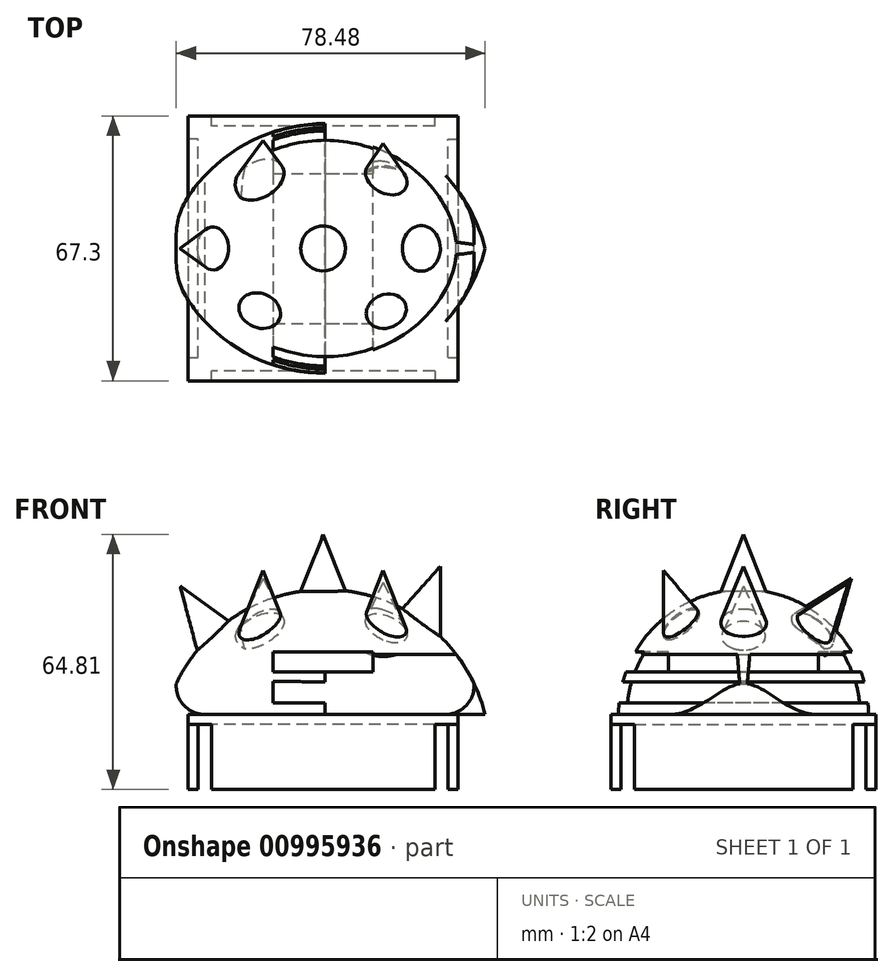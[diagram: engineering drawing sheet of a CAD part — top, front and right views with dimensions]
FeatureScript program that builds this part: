
annotation { "Feature Type Name" : "Feature", "Feature Type Description" : "" }
export const myFeature = defineFeature(function(context is Context, id is Id, definition is map)
    precondition{}
    {
        {
            var Q0;
            Q0=qCreatedBy(makeId("Front.planeOp"),FACE);
            var sketch = newSketch(context, id + "F0", { "sketchPlane" : qUnion([Q0])});
            skLineSegment(sketch, "E0", {"start": v(-40.15, 0) * mm, "end": v(41.13, 0) * mm});
            skLineSegment(sketch, "E1", {"start": v(0, 0) * mm, "end": v(0, 31.75) * mm});
            skArc(sketch, "E2", {"start": v(41.13, 0) * mm, "mid": v(0.5, 31.75) * mm, "end": v(-40.15, 0) * mm});
            skSolve(sketch);
        }
        {
            var Q0;
            {var subQ3=sQuery(id+"F0.wireOp",EDGE,"E1");Q0=makeQuery(id+"F0.imprint","IMPRINT",FACE,{"disambiguationData":[TD([[makeQuery(id+"F0.imprint","IMPRINT",EDGE,{"derivedFrom":subQ3}),-1.0]])]});}
            var Q1;
            {var subQ3=sQuery(id+"F0.wireOp",EDGE,"E1");Q1=makeQuery(id+"F0.imprint","IMPRINT",FACE,{"disambiguationData":[TD([[makeQuery(id+"F0.imprint","IMPRINT",EDGE,{"derivedFrom":subQ3}),1.0]])]});}
            var Q2;
            Q2=sQuery(id+"F0.wireOp",EDGE,"E0");
            revolve(context, id + "F1", {"surfaceOperationType" : NewSurfaceOperationType.NEW, "entities" : qUnion([Q0, Q1]), "axis" : qUnion([Q2]), "revolveType" : RevolveType.TWO_DIRECTIONS, "angle" : 90 * degree, "angleBack" : 270 * degree});
        }
        {
            var Q0;
            Q0=qCreatedBy(makeId("Front.planeOp"),FACE);
            var sketch = newSketch(context, id + "F2", { "sketchPlane" : qUnion([Q0])});
            skLineSegment(sketch, "E3.0.0", {"start": v(41.13, 0) * mm, "end": v(-40.15, 0) * mm});
            skLineSegment(sketch, "E3.0.1", {"start": v(-40.15, 0) * mm, "end": v(41.13, 0) * mm});
            skArc(sketch, "E4", {"start": v(41.13, 0) * mm, "mid": v(0.5, 31.65) * mm, "end": v(-40.15, 0) * mm});
            skArc(sketch, "E5", {"start": v(-37.33, 7.8) * mm, "mid": v(-35.4, 2.32) * mm, "end": v(-30.07, 0) * mm});
            skLineSegment(sketch, "E6", {"start": v(0.5, -10.26) * mm, "end": v(0.5, 25.68) * mm});
            skArc(sketch, "E7.MirrorCS", {"start": v(38.32, 7.8) * mm, "mid": v(36.38, 2.32) * mm, "end": v(31.06, 0) * mm});
            skLineSegment(sketch, "E8", {"start": v(-32.75, 15.27) * mm, "end": v(33.73, 15.27) * mm});
            skSolve(sketch);
        }
        {
            var Q0;
            {var subQ3=sQuery(id+"F2.wireOp",EDGE,"E7.MirrorCS");Q0=makeQuery(id+"F2.imprint","IMPRINT",FACE,{"disambiguationData":[TD([[makeQuery(id+"F2.imprint","IMPRINT",EDGE,{"derivedFrom":subQ3}),1.0]])]});}
            var Q1;
            {var subQ3=sQuery(id+"F2.wireOp",EDGE,"E5");Q1=makeQuery(id+"F2.imprint","IMPRINT",FACE,{"disambiguationData":[TD([[makeQuery(id+"F2.imprint","IMPRINT",EDGE,{"derivedFrom":subQ3}),-1.0]])]});}
            extrude(context, id + "F3", {"entities" : qUnion([Q0, Q1]), "operationType" : NewBodyOperationType.REMOVE, "endBound" : BoundingType.SYMMETRIC, "depth" : 127 * mm, "offsetDistance" : 25.4 * mm});
        }
        {
            var Q0;
            Q0=qCreatedBy(makeId("Top.planeOp"),FACE);
            var sketch = newSketch(context, id + "F4", { "sketchPlane" : qUnion([Q0])});
            skLineSegment(sketch, "E9.bottom", {"start": v(34.3, 33.66) * mm, "end": v(-34.3, 33.66) * mm});
            skLineSegment(sketch, "E9.top", {"start": v(34.3, -33.66) * mm, "end": v(-34.3, -33.66) * mm});
            skLineSegment(sketch, "E9.left", {"start": v(34.3, 33.66) * mm, "end": v(34.3, -33.66) * mm});
            skLineSegment(sketch, "E9.right", {"start": v(-34.3, 33.66) * mm, "end": v(-34.3, -33.66) * mm});
            skPoint(sketch, "E9.middle", {"position": v(0, 0) * mm});
            skSolve(sketch);
        }
        {
            var Q0;
            Q0=makeQuery(id+"F4.imprint","IMPRINT",FACE,{"disambiguationData":[TD([[makeQuery(id+"F4.imprint","IMPRINT",EDGE,{"derivedFrom":sQuery(id+"F4.wireOp",EDGE,"E9.bottom")}),1.0]])]});
            extrude(context, id + "F5", {"entities" : qUnion([Q0]), "operationType" : NewBodyOperationType.ADD, "oppositeDirection" : true, "depth" : 2.54 * mm, "offsetDistance" : 25.4 * mm});
        }
        {
            var Q0;
            Q0=makeQuery(id+"F5.opExtrude","CAP_FACE",FACE,{"disambiguationData":[OSD([sQuery(id+"F4.wireOp",EDGE,"E9.bottom"),sQuery(id+"F4.wireOp",EDGE,"E9.top"),sQuery(id+"F4.wireOp",EDGE,"E9.left"),sQuery(id+"F4.wireOp",EDGE,"E9.right")])],"isStart":false});
            var sketch = newSketch(context, id + "F6", { "sketchPlane" : qUnion([Q0])});
            skLineSegment(sketch, "E10.bottom", {"start": v(31.75, 31.12) * mm, "end": v(-31.75, 31.12) * mm});
            skLineSegment(sketch, "E10.top", {"start": v(31.75, -31.12) * mm, "end": v(-31.75, -31.12) * mm});
            skLineSegment(sketch, "E10.left", {"start": v(31.75, 31.12) * mm, "end": v(31.75, -31.12) * mm});
            skLineSegment(sketch, "E10.right", {"start": v(-31.75, 31.12) * mm, "end": v(-31.75, -31.12) * mm});
            skPoint(sketch, "E10.middle", {"position": v(0, 0) * mm});
            skLineSegment(sketch, "E11.0.0", {"start": v(34.3, 33.66) * mm, "end": v(-34.3, 33.66) * mm});
            skLineSegment(sketch, "E11.0.1", {"start": v(-34.3, 33.66) * mm, "end": v(-34.3, -33.66) * mm});
            skLineSegment(sketch, "E11.0.2", {"start": v(-34.3, -33.66) * mm, "end": v(34.3, -33.66) * mm});
            skLineSegment(sketch, "E11.0.3", {"start": v(34.3, -33.66) * mm, "end": v(34.3, 33.66) * mm});
            skSolve(sketch);
        }
        {
            var Q0;
            Q0=makeQuery(id+"F6.imprint","IMPRINT",FACE,{"disambiguationData":[TD([[makeQuery(id+"F6.imprint","IMPRINT",EDGE,{"derivedFrom":sQuery(id+"F6.wireOp",EDGE,"E10.bottom")}),-1.0]])]});
            extrude(context, id + "F7", {"entities" : qUnion([Q0]), "operationType" : NewBodyOperationType.ADD, "depth" : 16.5 * mm, "offsetDistance" : 25.4 * mm});
        }
        {
            var Q0;
            Q0=makeQuery(id+"F7.opExtrude","CAP_FACE",FACE,{"disambiguationData":[OSD([sQuery(id+"F6.wireOp",EDGE,"E10.bottom"),sQuery(id+"F6.wireOp",EDGE,"E10.top"),sQuery(id+"F6.wireOp",EDGE,"E10.left"),sQuery(id+"F6.wireOp",EDGE,"E10.right"),sQuery(id+"F6.wireOp",EDGE,"E11.0.0"),sQuery(id+"F6.wireOp",EDGE,"E11.0.1"),sQuery(id+"F6.wireOp",EDGE,"E11.0.2"),sQuery(id+"F6.wireOp",EDGE,"E11.0.3")])],"isStart":false});
            var sketch = newSketch(context, id + "F8", { "sketchPlane" : qUnion([Q0])});
            skLineSegment(sketch, "E12.0.0", {"start": v(34.3, -33.66) * mm, "end": v(34.3, 33.66) * mm});
            skLineSegment(sketch, "E12.0.1", {"start": v(34.3, 33.66) * mm, "end": v(-34.3, 33.66) * mm});
            skLineSegment(sketch, "E12.0.2", {"start": v(-34.3, 33.66) * mm, "end": v(-34.3, -33.66) * mm});
            skLineSegment(sketch, "E12.0.3", {"start": v(-34.3, -33.66) * mm, "end": v(34.3, -33.66) * mm});
            skLineSegment(sketch, "E13.0", {"start": v(31.75, 31.12) * mm, "end": v(-31.75, 31.12) * mm});
            skLineSegment(sketch, "E14.0", {"start": v(31.75, 31.12) * mm, "end": v(31.75, -31.12) * mm});
            skLineSegment(sketch, "E15.0.0", {"start": v(31.75, -31.12) * mm, "end": v(31.75, 31.12) * mm});
            skLineSegment(sketch, "E15.0.2", {"start": v(-31.75, 31.12) * mm, "end": v(-31.75, -31.12) * mm});
            skLineSegment(sketch, "E15.0.3", {"start": v(-31.75, -31.12) * mm, "end": v(31.75, -31.12) * mm});
            skLineSegment(sketch, "E16", {"start": v(31.75, 27.74) * mm, "end": v(34.3, 27.74) * mm});
            skLineSegment(sketch, "E17", {"start": v(28.37, 31.12) * mm, "end": v(28.37, 33.66) * mm});
            skLineSegment(sketch, "E18", {"start": v(-34.3, 27.74) * mm, "end": v(-31.75, 27.74) * mm});
            skLineSegment(sketch, "E19", {"start": v(-28.37, 33.66) * mm, "end": v(-28.37, 31.12) * mm});
            skLineSegment(sketch, "E20", {"start": v(-31.75, -27.74) * mm, "end": v(-34.3, -27.74) * mm});
            skLineSegment(sketch, "E21", {"start": v(-28.37, -31.12) * mm, "end": v(-28.37, -33.66) * mm});
            skLineSegment(sketch, "E22", {"start": v(31.75, -27.74) * mm, "end": v(34.3, -27.74) * mm});
            skLineSegment(sketch, "E23", {"start": v(28.37, -31.12) * mm, "end": v(28.37, -33.66) * mm});
            skSolve(sketch);
        }
        {
            var Q0;
            {var subQ4=sQuery(id+"F8.wireOp",EDGE,"E22");Q0=makeQuery(id+"F8.imprint","IMPRINT",FACE,{"disambiguationData":[TD([[makeQuery(id+"F8.imprint","IMPRINT",EDGE,{"derivedFrom":subQ4}),-1.0]])]});}
            var Q1;
            {var subQ7=sQuery(id+"F8.wireOp",EDGE,"E16");Q1=makeQuery(id+"F8.imprint","IMPRINT",FACE,{"disambiguationData":[TD([[makeQuery(id+"F8.imprint","IMPRINT",EDGE,{"derivedFrom":subQ7}),1.0]])]});}
            var Q2;
            {var subQ4=sQuery(id+"F8.wireOp",EDGE,"E18");Q2=makeQuery(id+"F8.imprint","IMPRINT",FACE,{"disambiguationData":[TD([[makeQuery(id+"F8.imprint","IMPRINT",EDGE,{"derivedFrom":subQ4}),1.0]])]});}
            var Q3;
            {var subQ4=sQuery(id+"F8.wireOp",EDGE,"E20");Q3=makeQuery(id+"F8.imprint","IMPRINT",FACE,{"disambiguationData":[TD([[makeQuery(id+"F8.imprint","IMPRINT",EDGE,{"derivedFrom":subQ4}),1.0]])]});}
            extrude(context, id + "F9", {"entities" : qUnion([Q0, Q1, Q2, Q3]), "operationType" : NewBodyOperationType.REMOVE, "oppositeDirection" : true, "depth" : 16.5 * mm, "offsetDistance" : 25.4 * mm});
        }
        {
            var Q0;
            Q0=qCreatedBy(makeId("Front.planeOp"),FACE);
            var sketch = newSketch(context, id + "F10", { "sketchPlane" : qUnion([Q0])});
            skPoint(sketch, "E24.middle", {"position": v(0, 12.77) * mm});
            skLineSegment(sketch, "E25", {"start": v(12.7, 10.84) * mm, "end": v(12.7, 15.92) * mm});
            skLineSegment(sketch, "E26.MirrorCS", {"start": v(-12.7, 10.84) * mm, "end": v(-12.7, 15.92) * mm});
            skLineSegment(sketch, "E27", {"start": v(-12.7, 10.84) * mm, "end": v(12.7, 10.84) * mm});
            skLineSegment(sketch, "E28", {"start": v(-12.7, 15.92) * mm, "end": v(12.7, 15.92) * mm});
            skPoint(sketch, "E29", {"position": v(0, 10.84) * mm});
            skSolve(sketch);
        }
        {
            var Q0;
            Q0=makeQuery(id+"F10.imprint","IMPRINT",FACE,{"disambiguationData":[TD([[makeQuery(id+"F10.imprint","IMPRINT",EDGE,{"derivedFrom":sQuery(id+"F10.wireOp",EDGE,"E25")}),1.0]])]});
            extrude(context, id + "F11", {"entities" : qUnion([Q0]), "operationType" : NewBodyOperationType.REMOVE, "endBound" : BoundingType.SYMMETRIC, "oppositeDirection" : true, "depth" : 76.2 * mm, "offsetDistance" : 25.4 * mm});
        }
        {
            var Q0;
            Q0=makeQuery(id+"F10.imprint","IMPRINT",FACE,{"disambiguationData":[TD([[makeQuery(id+"F10.imprint","IMPRINT",EDGE,{"derivedFrom":sQuery(id+"F10.wireOp",EDGE,"E25")}),1.0]])]});
            extrude(context, id + "F12", {"entities" : qUnion([Q0]), "operationType" : NewBodyOperationType.ADD, "endBound" : BoundingType.SYMMETRIC, "depth" : 38.1 * mm, "offsetDistance" : 25.4 * mm});
        }
        {
            var Q0;
            Q0=qCreatedBy(makeId("Front.planeOp"),FACE);
            var sketch = newSketch(context, id + "F13", { "sketchPlane" : qUnion([Q0])});
            skLineSegment(sketch, "E30", {"start": v(-12.7, 8.43) * mm, "end": v(-12.7, 2.93) * mm});
            skLineSegment(sketch, "E31", {"start": v(-12.7, 2.93) * mm, "end": v(12.74, 2.93) * mm});
            skLineSegment(sketch, "E32", {"start": v(12.74, 2.93) * mm, "end": v(12.74, 8.12) * mm});
            skLineSegment(sketch, "E33", {"start": v(12.74, 8.12) * mm, "end": v(-12.7, 8.43) * mm});
            skSolve(sketch);
        }
        {
            var Q0;
            Q0 = qSketchRegion(id + "F13", true);
            extrude(context, id + "F14", {"entities" : qUnion([Q0]), "operationType" : NewBodyOperationType.REMOVE, "oppositeDirection" : true, "depth" : 76.2 * mm, "offsetDistance" : 25.4 * mm});
        }
        {
            var Q0;
            Q0=makeQuery(id+"F14.boolean.opBoolean","COPY",FACE,{"derivedFrom":makeQuery(id+"F14.opExtrude","CAP_FACE",FACE,{"disambiguationData":[OSD([sQuery(id+"F13.wireOp",EDGE,"E30"),sQuery(id+"F13.wireOp",EDGE,"E31"),sQuery(id+"F13.wireOp",EDGE,"E32"),sQuery(id+"F13.wireOp",EDGE,"E33")])],"isStart":true})});
            extrude(context, id + "F15", {"entities" : qUnion([Q0]), "operationType" : NewBodyOperationType.REMOVE, "oppositeDirection" : true, "depth" : 50.8 * mm, "offsetDistance" : 25.4 * mm});
        }
        {
            var Q0;
            Q0=qCreatedBy(makeId("Front.planeOp"),FACE);
            var sketch = newSketch(context, id + "F16", { "sketchPlane" : qUnion([Q0])});
            skLineSegment(sketch, "E34", {"start": v(0, 27.42) * mm, "end": v(0, 45.76) * mm});
            skLineSegment(sketch, "E35", {"start": v(0, 45.76) * mm, "end": v(-7.24, 27.42) * mm});
            skLineSegment(sketch, "E36", {"start": v(-7.24, 27.42) * mm, "end": v(0, 27.42) * mm});
            skLineSegment(sketch, "E37", {"start": v(-27.22, 19.35) * mm, "end": v(-36.19, 32.44) * mm});
            skLineSegment(sketch, "E38", {"start": v(-36.28, 32.38) * mm, "end": v(-31.23, 13.34) * mm});
            skLineSegment(sketch, "E39", {"start": v(-31.23, 13.34) * mm, "end": v(-27.22, 19.35) * mm});
            skPoint(sketch, "E40.visualSharp", {"position": v(-36.36, 32.7) * mm});
            skLineSegment(sketch, "E41", {"start": v(-36.28, 32.38) * mm, "end": v(-36.19, 32.44) * mm});
            skLineSegment(sketch, "E42", {"start": v(29.77, 37.65) * mm, "end": v(23.8, 22.03) * mm});
            skLineSegment(sketch, "E43", {"start": v(29.77, 37.65) * mm, "end": v(29.77, 17.94) * mm});
            skLineSegment(sketch, "E44", {"start": v(29.77, 17.94) * mm, "end": v(23.8, 22.03) * mm});
            skSolve(sketch);
        }
        {
            var Q0;
            Q0=makeQuery(id+"F16.imprint","IMPRINT",FACE,{"disambiguationData":[TD([[makeQuery(id+"F16.imprint","IMPRINT",EDGE,{"derivedFrom":sQuery(id+"F16.wireOp",EDGE,"E37")}),1.0]])]});
            var Q1;
            Q1=sQuery(id+"F16.wireOp",EDGE,"E37");
            revolve(context, id + "F17", {"operationType" : NewBodyOperationType.ADD, "surfaceOperationType" : NewSurfaceOperationType.NEW, "entities" : qUnion([Q0]), "axis" : qUnion([Q1]), "revolveType" : RevolveType.FULL});
        }
        {
            var Q0;
            Q0=makeQuery(id+"F17.opRevolve","SWEPT_EDGE",EDGE,{"disambiguationData":[OSD([sQuery(id+"F16.wireOp",EDGE,"E38"),sQuery(id+"F16.wireOp",EDGE,"E41")])]});
            fillet(context, id + "F18", {"entities" : qUnion([Q0]), "tangentPropagation" : true, "radius" : 0.1 * mm, "defaultsChanged" : true, "vertexSettings" : [], "allowEdgeOverflow" : false});
        }
        {
            var Q0;
            Q0=qCreatedBy(makeId("Right.planeOp"),FACE);
            cPlane(context, id + "F19", {"entities" : qUnion([Q0]), "cplaneType" : CPlaneType.OFFSET, "offset" : 15.24 * mm, "oppositeDirection" : true, "width" : 152.4 * mm, "height" : 152.4 * mm});
        }
        {
            var Q0;
            Q0=qCreatedBy(id+"F19.planeOp",FACE);
            var sketch = newSketch(context, id + "F20", { "sketchPlane" : qUnion([Q0])});
            skLineSegment(sketch, "E45", {"start": v(17.1, 20.97) * mm, "end": v(27.4, 34.53) * mm});
            skLineSegment(sketch, "E46", {"start": v(27.4, 34.53) * mm, "end": v(21.94, 15.6) * mm});
            skLineSegment(sketch, "E47", {"start": v(21.94, 15.6) * mm, "end": v(17.1, 20.97) * mm});
            skLineSegment(sketch, "E48", {"start": v(-14.76, 21.53) * mm, "end": v(-20.33, 36.62) * mm});
            skLineSegment(sketch, "E49", {"start": v(-20.33, 36.62) * mm, "end": v(-20.33, 16.91) * mm});
            skLineSegment(sketch, "E50", {"start": v(-20.33, 16.91) * mm, "end": v(-14.76, 21.53) * mm});
            skSolve(sketch);
        }
        {
            var Q0;
            Q0=makeQuery(id+"F16.imprint","IMPRINT",FACE,{"disambiguationData":[TD([[makeQuery(id+"F16.imprint","IMPRINT",EDGE,{"derivedFrom":sQuery(id+"F16.wireOp",EDGE,"E34")}),1.0]])]});
            var Q1;
            Q1=sQuery(id+"F16.wireOp",EDGE,"E34");
            revolve(context, id + "F21", {"operationType" : NewBodyOperationType.ADD, "surfaceOperationType" : NewSurfaceOperationType.NEW, "entities" : qUnion([Q0]), "axis" : qUnion([Q1]), "revolveType" : RevolveType.FULL});
        }
        {
            var Q0;
            Q0=makeQuery(id+"F20.imprint","IMPRINT",FACE,{"disambiguationData":[TD([[makeQuery(id+"F20.imprint","IMPRINT",EDGE,{"derivedFrom":sQuery(id+"F20.wireOp",EDGE,"E45")}),-1.0]])]});
            var Q1;
            Q1=sQuery(id+"F20.wireOp",EDGE,"E45");
            revolve(context, id + "F22", {"operationType" : NewBodyOperationType.ADD, "surfaceOperationType" : NewSurfaceOperationType.NEW, "entities" : qUnion([Q0]), "axis" : qUnion([Q1]), "revolveType" : RevolveType.FULL});
        }
        {
            var Q0;
            Q0=makeQuery(id+"F16.imprint","IMPRINT",FACE,{"disambiguationData":[TD([[makeQuery(id+"F16.imprint","IMPRINT",EDGE,{"derivedFrom":sQuery(id+"F16.wireOp",EDGE,"E42")}),1.0]])]});
            var Q1;
            Q1=sQuery(id+"F16.wireOp",EDGE,"E42");
            revolve(context, id + "F23", {"operationType" : NewBodyOperationType.ADD, "surfaceOperationType" : NewSurfaceOperationType.NEW, "entities" : qUnion([Q0]), "axis" : qUnion([Q1]), "revolveType" : RevolveType.FULL});
        }
        {
            var Q0;
            Q0=makeQuery(id+"F20.imprint","IMPRINT",FACE,{"disambiguationData":[TD([[makeQuery(id+"F20.imprint","IMPRINT",EDGE,{"derivedFrom":sQuery(id+"F20.wireOp",EDGE,"E48")}),1.0]])]});
            var Q1;
            Q1=sQuery(id+"F20.wireOp",EDGE,"E48");
            revolve(context, id + "F24", {"operationType" : NewBodyOperationType.ADD, "surfaceOperationType" : NewSurfaceOperationType.NEW, "entities" : qUnion([Q0]), "axis" : qUnion([Q1]), "revolveType" : RevolveType.FULL});
        }
        {
            var Q0;
            Q0=qCreatedBy(makeId("Right.planeOp"),FACE);
            cPlane(context, id + "F25", {"entities" : qUnion([Q0]), "cplaneType" : CPlaneType.OFFSET, "offset" : 15.24 * mm, "width" : 152.4 * mm, "height" : 152.4 * mm});
        }
        {
            var Q0;
            Q0=qCreatedBy(id+"F25.planeOp",FACE);
            var sketch = newSketch(context, id + "F26", { "sketchPlane" : qUnion([Q0])});
            skLineSegment(sketch, "E51", {"start": v(17.1, 20.97) * mm, "end": v(26.68, 33.6) * mm});
            skLineSegment(sketch, "E52", {"start": v(26.68, 33.6) * mm, "end": v(20.83, 14.77) * mm});
            skLineSegment(sketch, "E53", {"start": v(20.83, 14.77) * mm, "end": v(17.1, 20.97) * mm});
            skLineSegment(sketch, "E54.0", {"start": v(17.1, 20.97) * mm, "end": v(27.4, 34.53) * mm});
            skLineSegment(sketch, "E55.0", {"start": v(-14.76, 21.53) * mm, "end": v(-20.33, 36.62) * mm});
            skLineSegment(sketch, "E56", {"start": v(-20.33, 36.62) * mm, "end": v(-14.76, 21.53) * mm});
            skLineSegment(sketch, "E57", {"start": v(-20.33, 36.62) * mm, "end": v(-20.33, 16.91) * mm});
            skLineSegment(sketch, "E58", {"start": v(-20.33, 16.91) * mm, "end": v(-14.76, 21.53) * mm});
            skSolve(sketch);
        }
        {
            var Q0;
            Q0=makeQuery(id+"F26.imprint","IMPRINT",FACE,{"disambiguationData":[TD([[makeQuery(id+"F26.imprint","IMPRINT",EDGE,{"derivedFrom":sQuery(id+"F26.wireOp",EDGE,"E51")}),-1.0]])]});
            var Q1;
            Q1=sQuery(id+"F26.wireOp",EDGE,"E54.0");
            revolve(context, id + "F27", {"operationType" : NewBodyOperationType.ADD, "surfaceOperationType" : NewSurfaceOperationType.NEW, "entities" : qUnion([Q0]), "axis" : qUnion([Q1]), "revolveType" : RevolveType.FULL});
        }
        {
            var Q0;
            Q0=makeQuery(id+"F26.imprint","IMPRINT",FACE,{"disambiguationData":[TD([[makeQuery(id+"F26.imprint","IMPRINT",EDGE,{"derivedFrom":sQuery(id+"F26.wireOp",EDGE,"E55.0")}),1.0]])]});
            var Q1;
            Q1=sQuery(id+"F26.wireOp",EDGE,"E55.0");
            revolve(context, id + "F28", {"operationType" : NewBodyOperationType.ADD, "surfaceOperationType" : NewSurfaceOperationType.NEW, "entities" : qUnion([Q0]), "axis" : qUnion([Q1]), "revolveType" : RevolveType.FULL});
        }
    });
